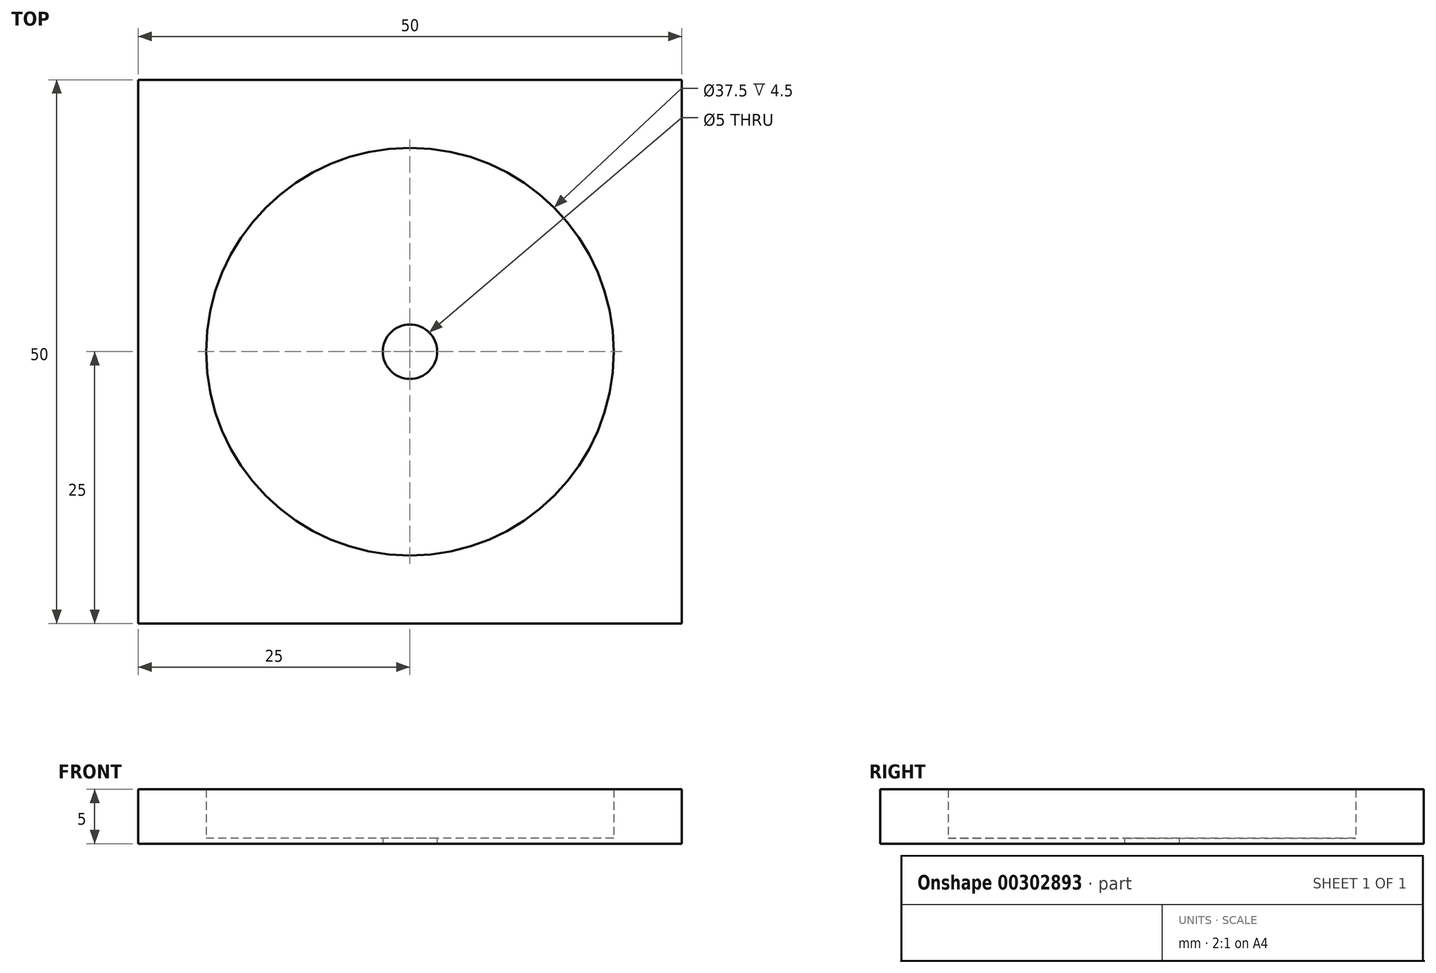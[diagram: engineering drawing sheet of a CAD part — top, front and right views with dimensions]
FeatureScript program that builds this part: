
annotation { "Feature Type Name" : "Feature", "Feature Type Description" : "" }
export const myFeature = defineFeature(function(context is Context, id is Id, definition is map)
    precondition{}
    {
        {
            var Q0;
            Q0=qCreatedBy(makeId("Top.planeOp"),FACE);
            var sketch = newSketch(context, id + "F0", { "sketchPlane" : qUnion([Q0])});
            skLineSegment(sketch, "E0.bottom", {"start": v(25, 25) * mm, "end": v(-25, 25) * mm});
            skLineSegment(sketch, "E0.top", {"start": v(25, -25) * mm, "end": v(-25, -25) * mm});
            skLineSegment(sketch, "E0.left", {"start": v(25, 25) * mm, "end": v(25, -25) * mm});
            skLineSegment(sketch, "E0.right", {"start": v(-25, 25) * mm, "end": v(-25, -25) * mm});
            skPoint(sketch, "E0.middle", {"position": v(0, 0) * mm});
            skCircle(sketch, "E1", {"center": v(0, 0) * mm, "radius": 18.75 * mm});
            skCircle(sketch, "E2", {"center": v(0, 0) * mm, "radius": 2.5 * mm});
            skSolve(sketch);
        }
        {
            var Q0;
            Q0=makeQuery(id+"F0.imprint","IMPRINT",FACE,{"disambiguationData":[TD([[makeQuery(id+"F0.imprint","IMPRINT",EDGE,{"derivedFrom":sQuery(id+"F0.wireOp",EDGE,"E0.bottom")}),1.0]])]});
            extrude(context, id + "F1", {"entities" : qUnion([Q0]), "depth" : 5 * mm});
        }
        {
            var Q0;
            Q0=makeQuery(id+"F0.imprint","IMPRINT",FACE,{"disambiguationData":[TD([[makeQuery(id+"F0.imprint","IMPRINT",EDGE,{"derivedFrom":sQuery(id+"F0.wireOp",EDGE,"E1")}),1.0]])]});
            extrude(context, id + "F2", {"entities" : qUnion([Q0]), "operationType" : NewBodyOperationType.ADD, "depth" : .5 * mm});
        }
    });
